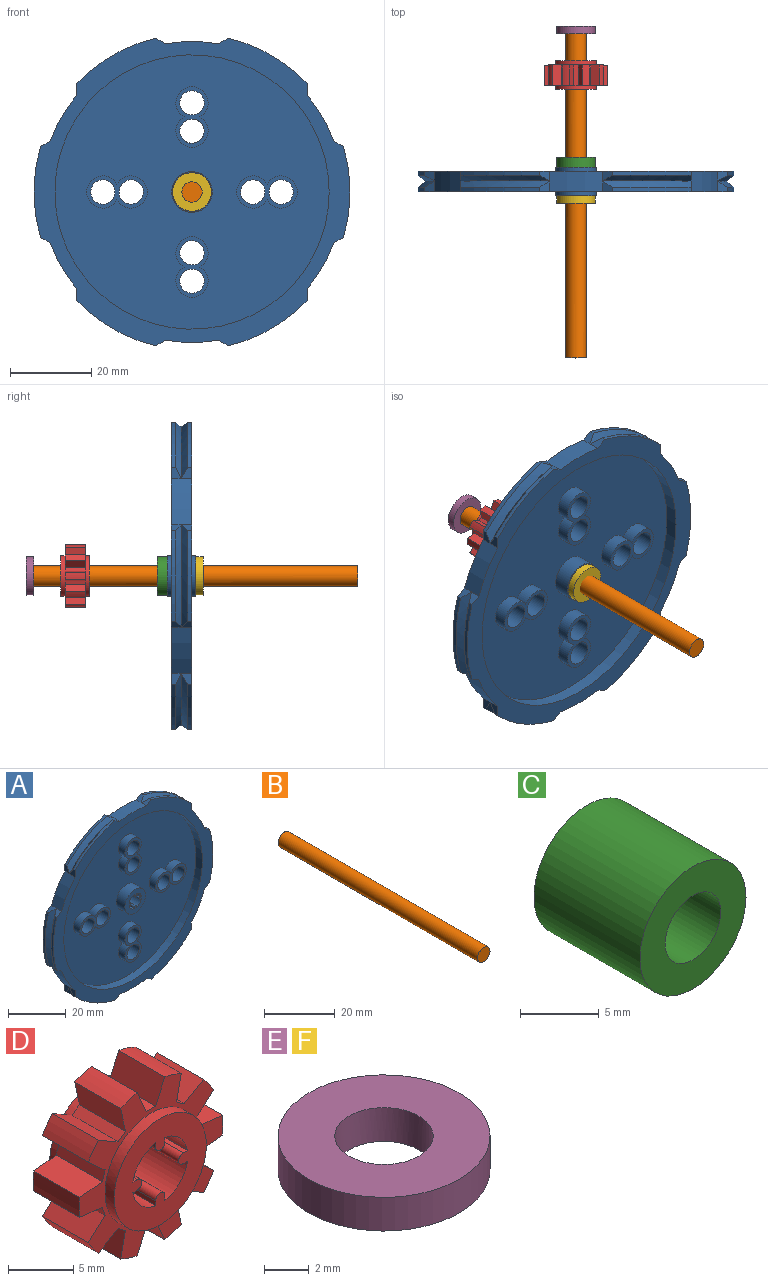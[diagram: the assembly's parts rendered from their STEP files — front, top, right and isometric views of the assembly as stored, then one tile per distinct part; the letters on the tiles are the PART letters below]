
ASSEMBLY  parts=6 mates=5
PART A: 98 faces, bbox 78x7x76.7 mm
  f0: plane 14.97x7.98mm, normal (0,-1,0), area 40.9mm2, adj f29,f32,f88,f92
  f1: plane 14.97x7.98mm, normal (0,-1,0), area 40.9mm2, adj f28,f47,f89,f93
  f2: plane 14.97x7.98mm, normal (0,-1,0), area 40.9mm2, adj f31,f34,f90,f94
  f3: plane 14.97x7.98mm, normal (0,-1,0), area 40.9mm2, adj f30,f55,f91,f95
  f4: plane 77.96x75.87mm, normal (0,1,0), area 4294.7mm2, adj f6,f10,f14,f18,f22,f26,f28,f29
  f5: cylinder r=38.98mm len=19.42mm, axis (0,-1,0), area 23.1mm2, adj f27,f56,f59,f86
  f6: cylinder r=38.98mm len=19.42mm, axis (0,-1,0), area 23.1mm2, adj f4,f57,f60,f87
  f7: cone r=37.13mm half-angle=49.6deg, axis (0,-1,0), area 59mm2, adj f8,f9,f81,f84
  f8: cone r=38.98mm half-angle=53.2deg, axis (0,1,0), area 56.1mm2, adj f7,f10,f82,f85
  f9: cylinder r=38.98mm len=22.42mm, axis (0,-1,0), area 23.1mm2, adj f7,f27,f81,f84
  f10: cylinder r=38.98mm len=22.42mm, axis (0,-1,0), area 23.1mm2, adj f4,f8,f82,f85
  f11: cone r=37.13mm half-angle=49.6deg, axis (0,-1,0), area 59mm2, adj f12,f13,f76,f79
  f12: cone r=38.98mm half-angle=53.2deg, axis (0,1,0), area 56.1mm2, adj f11,f14,f77,f80
  f13: cylinder r=38.98mm len=19.42mm, axis (0,-1,0), area 23.1mm2, adj f11,f27,f76,f79
  f14: cylinder r=38.98mm len=19.42mm, axis (0,-1,0), area 23.1mm2, adj f4,f12,f77,f80
  f15: cone r=37.13mm half-angle=49.6deg, axis (0,-1,0), area 59mm2, adj f16,f17,f71,f74
  f16: cone r=38.98mm half-angle=53.2deg, axis (0,1,0), area 56.1mm2, adj f15,f18,f72,f75
  f17: cylinder r=38.98mm len=19.42mm, axis (0,-1,0), area 23.1mm2, adj f15,f27,f71,f74
  f18: cylinder r=38.98mm len=19.42mm, axis (0,-1,0), area 23.1mm2, adj f4,f16,f72,f75
  f19: cone r=37.13mm half-angle=49.6deg, axis (0,-1,0), area 59mm2, adj f20,f21,f66,f69
  f20: cone r=38.98mm half-angle=53.2deg, axis (0,1,0), area 56.1mm2, adj f19,f22,f67,f70
  f21: cylinder r=38.98mm len=22.42mm, axis (0,-1,0), area 23.1mm2, adj f19,f27,f66,f69
  f22: cylinder r=38.98mm len=22.42mm, axis (0,-1,0), area 23.1mm2, adj f4,f20,f67,f70
  f23: cone r=37.13mm half-angle=49.6deg, axis (0,-1,0), area 59mm2, adj f24,f25,f61,f64
  f24: cone r=38.98mm half-angle=53.2deg, axis (0,1,0), area 56.1mm2, adj f23,f26,f62,f65
  f25: cylinder r=38.98mm len=19.42mm, axis (0,-1,0), area 23.1mm2, adj f23,f27,f61,f64
  f26: cylinder r=38.98mm len=19.42mm, axis (0,-1,0), area 23.1mm2, adj f4,f24,f62,f65
  f27: plane 77.96x75.87mm, normal (0,-1,0), area 1004.6mm2, adj f5,f9,f13,f17,f21,f25,f58,f59
  f28: cylinder r=3mm len=6mm, axis (0,1,0), area 94.2mm2, adj f1,f4
  f29: cylinder r=3mm len=6mm, axis (0,1,0), area 94.2mm2, adj f0,f4
  f30: cylinder r=3mm len=6mm, axis (0,1,0), area 94.2mm2, adj f3,f4
  f31: cylinder r=3mm len=6mm, axis (0,1,0), area 94.2mm2, adj f2,f4
  f32: cylinder r=3mm len=6mm, axis (0,-1,0), area 94.2mm2, adj f0,f4
  f33: cylinder r=3mm len=7mm, axis (0,-1,0), area 26mm2, adj f40,f42,f45,f48
  f34: cylinder r=3mm len=6mm, axis (0,-1,0), area 94.2mm2, adj f2,f4
  f35: cylinder r=5mm len=10mm, axis (0,1,0), area 131.2mm2, adj f42,f97
  f36: plane 7x0.46mm, normal (0,0,1), area 3.2mm2, adj f41,f42,f45,f51
  f37: plane 7x0.46mm, normal (-1,0,0), area 3.2mm2, adj f42,f43,f45,f50
  f38: plane 7x0.46mm, normal (1,0,0), area 3.2mm2, adj f42,f43,f45,f51
  f39: plane 7x0.46mm, normal (0,0,1), area 3.2mm2, adj f42,f45,f49,f50
  f40: plane 7x0.46mm, normal (-1,0,0), area 3.2mm2, adj f33,f42,f45,f54
  f41: cylinder r=0.5mm len=7mm, axis (0,1,0), area 11mm2, adj f36,f42,f44,f45
  f42: plane 10x10mm, normal (0,-1,0), area 53.8mm2, adj f33,f35,f36,f37,f38,f39,f40,f41
  f43: cylinder r=0.5mm len=7mm, axis (0,1,0), area 11mm2, adj f37,f38,f42,f45
  f44: plane 7x0.46mm, normal (0,0,-1), area 3.2mm2, adj f41,f42,f45,f52
  f45: plane 10x10mm, normal (0,1,0), area 53.8mm2, adj f33,f36,f37,f38,f39,f40,f41,f43
  f46: cylinder r=5mm len=10mm, axis (0,-1,0), area 31.4mm2, adj f4,f45
  f47: cylinder r=3mm len=6mm, axis (0,-1,0), area 94.2mm2, adj f1,f4
  f48: plane 7x0.46mm, normal (0,0,-1), area 3.2mm2, adj f33,f42,f45,f49
  f49: cylinder r=0.5mm len=7mm, axis (0,1,0), area 11mm2, adj f39,f42,f45,f48
  f50: cylinder r=3mm len=7mm, axis (0,-1,0), area 26mm2, adj f37,f39,f42,f45
  f51: cylinder r=3mm len=7mm, axis (0,-1,0), area 26mm2, adj f36,f38,f42,f45
  f52: cylinder r=3mm len=7mm, axis (0,-1,0), area 26mm2, adj f42,f44,f45,f53
  f53: plane 7x0.46mm, normal (1,0,0), area 3.2mm2, adj f42,f45,f52,f54
  f54: cylinder r=0.5mm len=7mm, axis (0,1,0), area 11mm2, adj f40,f42,f45,f53
  f55: cylinder r=3mm len=6mm, axis (0,-1,0), area 94.2mm2, adj f3,f4
  f56: cone r=37.13mm half-angle=49.6deg, axis (0,-1,0), area 59mm2, adj f5,f57,f59,f86
  f57: cone r=38.98mm half-angle=53.2deg, axis (0,1,0), area 56.1mm2, adj f6,f56,f60,f87
  f58: cylinder r=37.13mm len=13.09mm, axis (0,-1,0), area 65.8mm2, adj f4,f27,f59,f60,f61,f62
  f59: plane 2.6x2.41mm, normal (-0.5,0,0.87), area 5.1mm2, adj f5,f27,f56,f58
  f60: plane 2.41x2.4mm, normal (-0.5,0,0.87), area 4.8mm2, adj f4,f6,f57,f58
  f61: plane 2.6x2.41mm, normal (0.5,0,0.87), area 5.1mm2, adj f23,f25,f27,f58
  f62: plane 2.41x2.4mm, normal (0.5,0,0.87), area 4.8mm2, adj f4,f24,f26,f58
  f63: cylinder r=37.13mm len=11.34mm, axis (0,-1,0), area 65.8mm2, adj f4,f27,f64,f65,f66,f67
  f64: plane 2.79x2.6mm, normal (-1,0,0), area 5.1mm2, adj f23,f25,f27,f63
  f65: plane 2.79x2.41mm, normal (-1,0,0), area 4.8mm2, adj f4,f24,f26,f63
  f66: plane 2.6x2.41mm, normal (-0.5,0,0.87), area 5.1mm2, adj f19,f21,f27,f63
  f67: plane 2.41x2.4mm, normal (-0.5,0,0.87), area 4.8mm2, adj f4,f20,f22,f63
  f68: cylinder r=37.13mm len=11.34mm, axis (0,-1,0), area 65.8mm2, adj f4,f27,f69,f70,f71,f72
  f69: plane 2.6x2.41mm, normal (-0.5,0,-0.87), area 5.1mm2, adj f19,f21,f27,f68
  f70: plane 2.41x2.4mm, normal (-0.5,0,-0.87), area 4.8mm2, adj f4,f20,f22,f68
  f71: plane 2.79x2.6mm, normal (-1,0,0), area 5.1mm2, adj f15,f17,f27,f68
  f72: plane 2.79x2.41mm, normal (-1,0,0), area 4.8mm2, adj f4,f16,f18,f68
  f73: cylinder r=37.13mm len=13.09mm, axis (0,-1,0), area 65.8mm2, adj f4,f27,f74,f75,f76,f77
  f74: plane 2.6x2.41mm, normal (0.5,0,-0.87), area 5.1mm2, adj f15,f17,f27,f73
  f75: plane 2.41x2.4mm, normal (0.5,0,-0.87), area 4.8mm2, adj f4,f16,f18,f73
  f76: plane 2.6x2.41mm, normal (-0.5,0,-0.87), area 5.1mm2, adj f11,f13,f27,f73
  f77: plane 2.41x2.4mm, normal (-0.5,0,-0.87), area 4.8mm2, adj f4,f12,f14,f73
  f78: cylinder r=37.13mm len=11.34mm, axis (0,-1,0), area 65.8mm2, adj f4,f27,f79,f80,f81,f82
  f79: plane 2.79x2.6mm, normal (1,0,0), area 5.1mm2, adj f11,f13,f27,f78
  f80: plane 2.79x2.41mm, normal (1,0,0), area 4.8mm2, adj f4,f12,f14,f78
  f81: plane 2.6x2.41mm, normal (0.5,0,-0.87), area 5.1mm2, adj f7,f9,f27,f78
  f82: plane 2.41x2.4mm, normal (0.5,0,-0.87), area 4.8mm2, adj f4,f8,f10,f78
  f83: cylinder r=37.13mm len=11.34mm, axis (0,-1,0), area 65.8mm2, adj f4,f27,f84,f85,f86,f87
  f84: plane 2.6x2.41mm, normal (0.5,0,0.87), area 5.1mm2, adj f7,f9,f27,f83
  f85: plane 2.41x2.4mm, normal (0.5,0,0.87), area 4.8mm2, adj f4,f8,f10,f83
  f86: plane 2.79x2.6mm, normal (1,0,0), area 5.1mm2, adj f5,f27,f56,f83
  f87: plane 2.79x2.41mm, normal (1,0,0), area 4.8mm2, adj f4,f6,f57,f83
  f88: cylinder r=3.99mm len=7.98mm, axis (0,-1,0), area 66.8mm2, adj f0,f92,f97
  f89: cylinder r=3.99mm len=7.98mm, axis (0,-1,0), area 66.8mm2, adj f1,f93,f97
  f90: cylinder r=3.99mm len=7.98mm, axis (0,-1,0), area 66.8mm2, adj f2,f94,f97
  f91: cylinder r=3.99mm len=7.98mm, axis (0,-1,0), area 66.8mm2, adj f3,f95,f97
  f92: cylinder r=3.99mm len=7.98mm, axis (0,-1,0), area 66.8mm2, adj f0,f88,f97
  f93: cylinder r=3.99mm len=7.98mm, axis (0,-1,0), area 66.8mm2, adj f1,f89,f97
  f94: cylinder r=3.99mm len=7.98mm, axis (0,-1,0), area 66.8mm2, adj f2,f90,f97
  f95: cylinder r=3.99mm len=7.98mm, axis (0,-1,0), area 66.8mm2, adj f3,f91,f97
  f96: cylinder r=33.83mm len=67.65mm, axis (0,-1,0), area 674.8mm2, adj f27,f97
  f97: plane 67.65x67.65mm, normal (0,-1,0), area 3126.7mm2, adj f35,f88,f89,f90,f91,f92,f93,f94
PART B: 3 faces, bbox 5x80x5 mm
  f0: plane 5x5mm, normal (0,1,0), area 19.6mm2, adj f1
  f1: cylinder r=2.5mm len=80mm, axis (0,-1,0), area 1256.6mm2, adj f0,f2
  f2: plane 5x5mm, normal (0,-1,0), area 19.6mm2, adj f1
PART C: 4 faces, bbox 9.5x9.5x9.5 mm
  f0: cylinder r=2.5mm len=9.53mm, axis (0,1,0), area 149.6mm2, adj f2,f3
  f1: cylinder r=4.76mm len=9.53mm, axis (0,1,0), area 285mm2, adj f2,f3
  f2: plane 9.53x9.53mm, normal (0,-1,0), area 51.6mm2, adj f0,f1
  f3: plane 9.53x9.53mm, normal (0,1,0), area 51.6mm2, adj f0,f1
PART D: 62 faces, bbox 15.6x7x15.3 mm
  f0: plane 15.6x15.31mm, normal (0,1,0), area 64.7mm2, adj f1,f7,f8,f9,f10,f11,f12,f13
  f1: cylinder r=5mm len=10mm, axis (0,1,0), area 31.4mm2, adj f0,f2
  f2: plane 10x10mm, normal (0,1,0), area 53.8mm2, adj f1,f3,f47,f48,f49,f50,f51,f52
  f3: cylinder r=0.5mm len=7mm, axis (0,-1,0), area 11mm2, adj f2,f4,f47,f58
  f4: plane 10x10mm, normal (0,-1,0), area 53.8mm2, adj f3,f5,f47,f48,f49,f50,f51,f52
  f5: cylinder r=5mm len=10mm, axis (0,-1,0), area 31.4mm2, adj f4,f6
  f6: plane 15.6x15.31mm, normal (0,-1,0), area 64.7mm2, adj f5,f7,f8,f9,f10,f11,f12,f13
  f7: plane 5x0.81mm, normal (-0.59,0,0.81), area 5mm2, adj f0,f6,f8,f46
  f8: plane 5x2.41mm, normal (-0.98,0,-0.21), area 12.3mm2, adj f0,f6,f7,f18
  f9: cylinder r=7.8mm len=5mm, axis (0,-1,0), area 9.4mm2, adj f0,f6,f19,f22
  f10: cylinder r=7.8mm len=5mm, axis (0,-1,0), area 9.4mm2, adj f0,f6,f21,f25
  f11: cylinder r=7.8mm len=5mm, axis (0,-1,0), area 9.4mm2, adj f0,f6,f27,f28
  f12: cylinder r=7.8mm len=5mm, axis (0,-1,0), area 9.4mm2, adj f0,f6,f30,f31
  f13: cylinder r=7.8mm len=5mm, axis (0,-1,0), area 9.4mm2, adj f0,f6,f33,f34
  f14: cylinder r=7.8mm len=5mm, axis (0,-1,0), area 9.4mm2, adj f0,f6,f36,f37
  f15: cylinder r=7.8mm len=5mm, axis (0,-1,0), area 9.4mm2, adj f0,f6,f39,f40
  f16: cylinder r=7.8mm len=5mm, axis (0,-1,0), area 9.4mm2, adj f0,f6,f42,f43
  f17: cylinder r=7.8mm len=5mm, axis (0,-1,0), area 9.4mm2, adj f0,f6,f45,f46
  f18: cylinder r=7.8mm len=5mm, axis (0,-1,0), area 9.4mm2, adj f0,f6,f8,f24
  f19: plane 5x2.41mm, normal (0.98,0,-0.21), area 12.3mm2, adj f0,f6,f9,f20
  f20: plane 5x0.81mm, normal (0.59,0,0.81), area 5mm2, adj f0,f6,f19,f21
  f21: plane 5x2.13mm, normal (-0.5,0,0.87), area 12.3mm2, adj f0,f6,f10,f20
  f22: plane 5x2.25mm, normal (-0.91,0,0.41), area 12.3mm2, adj f0,f6,f9,f23
  f23: plane 5x1mm, normal (0,0,1), area 5mm2, adj f0,f6,f22,f24
  f24: plane 5x2.25mm, normal (0.91,0,0.41), area 12.3mm2, adj f0,f6,f18,f23
  f25: plane 5x1.83mm, normal (0.67,0,-0.74), area 12.3mm2, adj f0,f6,f10,f26
  f26: plane 5x0.95mm, normal (0.95,0,0.31), area 5mm2, adj f0,f6,f25,f27
  f27: plane 5x2.45mm, normal (0.1,0,0.99), area 12.3mm2, adj f0,f6,f11,f26
  f28: plane 5x2.45mm, normal (0.1,0,-0.99), area 12.3mm2, adj f0,f6,f11,f29
  f29: plane 5x0.95mm, normal (0.95,0,-0.31), area 5mm2, adj f0,f6,f28,f30
  f30: plane 5x1.83mm, normal (0.67,0,0.74), area 12.3mm2, adj f0,f6,f12,f29
  f31: plane 5x2.13mm, normal (-0.5,0,-0.87), area 12.3mm2, adj f0,f6,f12,f32
  f32: plane 5x0.81mm, normal (0.59,0,-0.81), area 5mm2, adj f0,f6,f31,f33
  f33: plane 5x2.41mm, normal (0.98,0,0.21), area 12.3mm2, adj f0,f6,f13,f32
  f34: plane 5x2.25mm, normal (-0.91,0,-0.41), area 12.3mm2, adj f0,f6,f13,f35
  f35: plane 5x1mm, normal (0,0,-1), area 5mm2, adj f0,f6,f34,f36
  f36: plane 5x2.25mm, normal (0.91,0,-0.41), area 12.3mm2, adj f0,f6,f14,f35
  f37: plane 5x2.41mm, normal (-0.98,0,0.21), area 12.3mm2, adj f0,f6,f14,f38
  f38: plane 5x0.81mm, normal (-0.59,0,-0.81), area 5mm2, adj f0,f6,f37,f39
  f39: plane 5x2.13mm, normal (0.5,0,-0.87), area 12.3mm2, adj f0,f6,f15,f38
  f40: plane 5x1.83mm, normal (-0.67,0,0.74), area 12.3mm2, adj f0,f6,f15,f41
  f41: plane 5x0.95mm, normal (-0.95,0,-0.31), area 5mm2, adj f0,f6,f40,f42
  f42: plane 5x2.45mm, normal (-0.1,0,-0.99), area 12.3mm2, adj f0,f6,f16,f41
  f43: plane 5x2.45mm, normal (-0.1,0,0.99), area 12.3mm2, adj f0,f6,f16,f44
  f44: plane 5x0.95mm, normal (-0.95,0,0.31), area 5mm2, adj f0,f6,f43,f45
  f45: plane 5x1.83mm, normal (-0.67,0,-0.74), area 12.3mm2, adj f0,f6,f17,f44
  f46: plane 5x2.13mm, normal (0.5,0,0.87), area 12.3mm2, adj f0,f6,f7,f17
  f47: plane 7x0.46mm, normal (-1,0,0), area 3.2mm2, adj f2,f3,f4,f48
  f48: cylinder r=3mm len=7mm, axis (0,1,0), area 26mm2, adj f2,f4,f47,f52
  f49: cylinder r=3mm len=7mm, axis (0,1,0), area 26mm2, adj f2,f4,f55,f58
  f50: cylinder r=3mm len=7mm, axis (0,1,0), area 26mm2, adj f2,f4,f57,f59
  f51: cylinder r=3mm len=7mm, axis (0,1,0), area 26mm2, adj f2,f4,f54,f61
  f52: plane 7x0.46mm, normal (0,0,1), area 3.2mm2, adj f2,f4,f48,f53
  f53: cylinder r=0.5mm len=7mm, axis (0,-1,0), area 11mm2, adj f2,f4,f52,f54
  f54: plane 7x0.46mm, normal (0,0,-1), area 3.2mm2, adj f2,f4,f51,f53
  f55: plane 7x0.46mm, normal (0,0,1), area 3.2mm2, adj f2,f4,f49,f56
  f56: cylinder r=0.5mm len=7mm, axis (0,-1,0), area 11mm2, adj f2,f4,f55,f57
  f57: plane 7x0.46mm, normal (0,0,-1), area 3.2mm2, adj f2,f4,f50,f56
  f58: plane 7x0.46mm, normal (1,0,0), area 3.2mm2, adj f2,f3,f4,f49
  f59: plane 7x0.46mm, normal (1,0,0), area 3.2mm2, adj f2,f4,f50,f60
  f60: cylinder r=0.5mm len=7mm, axis (0,-1,0), area 11mm2, adj f2,f4,f59,f61
  f61: plane 7x0.46mm, normal (-1,0,0), area 3.2mm2, adj f2,f4,f51,f60
PART E: 4 faces, bbox 9.5x9.5x1.9 mm
  f0: cylinder r=2.21mm len=4.42mm, axis (0,0,1), area 25.7mm2, adj f1,f3
  f1: plane 9.53x9.53mm, normal (0,0,-1), area 55.9mm2, adj f0,f2
  f2: cylinder r=4.76mm len=9.53mm, axis (0,0,-1), area 55.5mm2, adj f1,f3
  f3: plane 9.53x9.53mm, normal (0,0,1), area 55.9mm2, adj f0,f2
PART F: same geometry as E
PLACE A t=(34.76,20.55,-11.92)mm
PLACE B t=(34.76,54.55,-11.92)mm
PLACE C t=(34.76,24.08,-11.92)mm
PLACE D rot(axis=(1,0,0),180deg) t=(34.76,41.79,-11.92)mm
PLACE E rot(axis=(1,0,0),90deg) t=(34.76,56.4,-11.92)mm
PLACE F rot(axis=(1,0,0),90deg) t=(34.76,14.55,-11.92)mm
MATE cylindrical A.f5 <-> B.f1  axis (0,-1,0) through (34.76,14.55,-11.92)mm
MATE cylindrical E.f0 <-> B.f1  axis (0,-1,0) through (34.76,54.55,-11.92)mm
MATE cylindrical D.f1 <-> B.f1  axis (0,-1,0) through (34.76,40.79,-11.92)mm
MATE cylindrical F.f0 <-> B.f1  axis (0,1,0) through (34.76,14.55,-11.92)mm
MATE cylindrical C.f0 <-> B.f1  axis (0,-1,0) through (34.76,14.55,-11.92)mm
